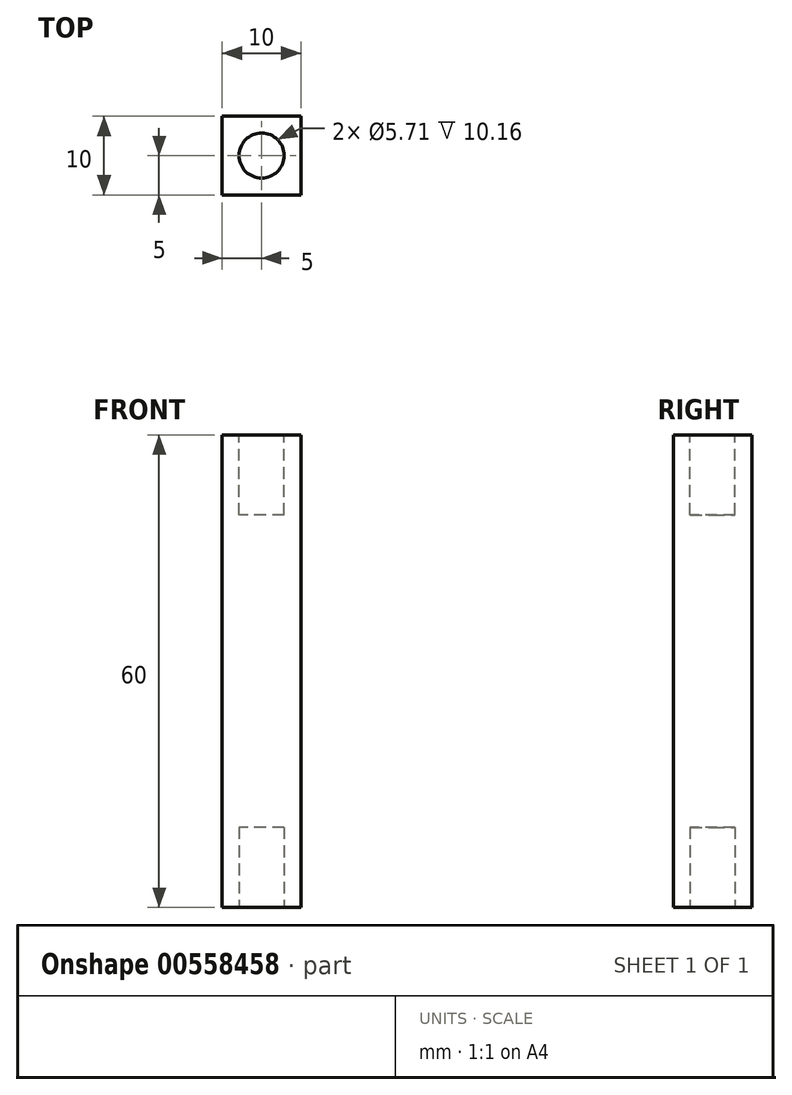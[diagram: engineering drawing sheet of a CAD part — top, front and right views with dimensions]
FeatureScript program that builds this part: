
annotation { "Feature Type Name" : "Feature", "Feature Type Description" : "" }
export const myFeature = defineFeature(function(context is Context, id is Id, definition is map)
    precondition{}
    {
        {
            var Q0;
            Q0=qCreatedBy(makeId("Top.planeOp"),FACE);
            var sketch = newSketch(context, id + "F0", { "sketchPlane" : qUnion([Q0])});
            skLineSegment(sketch, "E0.bottom", {"start": v(5, -5) * mm, "end": v(-5, -5) * mm});
            skLineSegment(sketch, "E0.top", {"start": v(5, 5) * mm, "end": v(-5, 5) * mm});
            skLineSegment(sketch, "E0.left", {"start": v(5, -5) * mm, "end": v(5, 5) * mm});
            skLineSegment(sketch, "E0.right", {"start": v(-5, -5) * mm, "end": v(-5, 5) * mm});
            skPoint(sketch, "E0.middle", {"position": v(0, 0) * mm});
            skSolve(sketch);
        }
        {
            var Q0;
            Q0=makeQuery(id+"F0.imprint","IMPRINT",FACE,{"disambiguationData":[TD([[makeQuery(id+"F0.imprint","IMPRINT",EDGE,{"derivedFrom":sQuery(id+"F0.wireOp",EDGE,"E0.bottom")}),-1.0]])]});
            extrude(context, id + "F1", {"entities" : qUnion([Q0]), "depth" : 60 * mm, "offsetDistance" : 25 * mm});
        }
        {
            var Q0;
            Q0=qCreatedBy(makeId("Top.planeOp"),FACE);
            var sketch = newSketch(context, id + "F2", { "sketchPlane" : qUnion([Q0])});
            skCircle(sketch, "E1", {"center": v(0, 0) * mm, "radius": 2.86 * mm});
            skSolve(sketch);
        }
        {
            var Q0;
            Q0=makeQuery(id+"F2.imprint","IMPRINT",FACE,{"disambiguationData":[TD([[makeQuery(id+"F2.imprint","IMPRINT",EDGE,{"derivedFrom":sQuery(id+"F2.wireOp",EDGE,"E1")}),1.0]])]});
            extrude(context, id + "F3", {"entities" : qUnion([Q0]), "operationType" : NewBodyOperationType.REMOVE, "depth" : 10.16 * mm, "offsetDistance" : 25.4 * mm});
        }
        {
            var Q0;
            Q0=makeQuery(id+"F1.opExtrude","CAP_FACE",FACE,{"disambiguationData":[OSD([sQuery(id+"F0.wireOp",EDGE,"E0.bottom"),sQuery(id+"F0.wireOp",EDGE,"E0.top"),sQuery(id+"F0.wireOp",EDGE,"E0.left"),sQuery(id+"F0.wireOp",EDGE,"E0.right")])],"isStart":false});
            var sketch = newSketch(context, id + "F4", { "sketchPlane" : qUnion([Q0])});
            skCircle(sketch, "E2", {"center": v(0, 0) * mm, "radius": 2.86 * mm});
            skSolve(sketch);
        }
        {
            var Q0;
            Q0=makeQuery(id+"F4.imprint","IMPRINT",FACE,{"disambiguationData":[TD([[makeQuery(id+"F4.imprint","IMPRINT",EDGE,{"derivedFrom":sQuery(id+"F4.wireOp",EDGE,"E2")}),1.0]])]});
            extrude(context, id + "F5", {"entities" : qUnion([Q0]), "operationType" : NewBodyOperationType.REMOVE, "oppositeDirection" : true, "depth" : 10.16 * mm, "offsetDistance" : 25.4 * mm});
        }
    });
